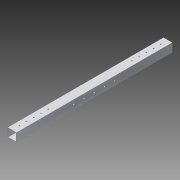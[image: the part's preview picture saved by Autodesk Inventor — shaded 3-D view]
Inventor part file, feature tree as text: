
AUTODESK INVENTOR PART (.ipt)
format: ipt  version: 2015 (Build 190159000, 159)  size: 188,928 bytes
history: native  units: in
note: dims shown in document units (in); Inventor stores cm internally (conversion verified against a paired STEP export)
features: other x4, hole x3, projected_geometry x2, extrude x1
ambient origin geometry x8: Origin, YZ Plane, XZ Plane, XY Plane, X Axis, Y Axis, Z Axis, Center Point
bodies: Solid1 (feature_tree)
feature tree (10):
  extrude  "profile_extrusion"  Depth=1.0in
  hole  "tb_rivet_holes"  [1 undecoded]
  hole  "bh_rivet_holes"  [1 undecoded]
  hole  "pdb_ziptie_holes"  [1 undecoded]
  other  "profile_sketch"
  other  "rivet_holes_sketch"
  other  "bh_rivet_holes_sketch"
  projected_geometry  "Projected Loop1"
  other  "pdb_ziptie_sketch"
  projected_geometry  "Projected Loop2"
note: 3 required parameter values undecoded (feature->parameter linkage not recoverable at this tier; creation-order binding heuristic only, values carry confidence <= 0.55)
